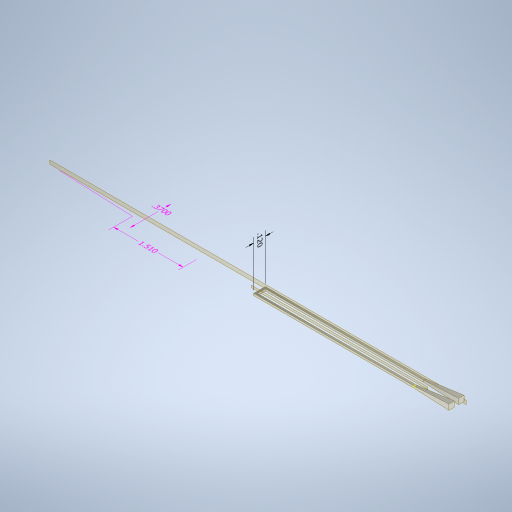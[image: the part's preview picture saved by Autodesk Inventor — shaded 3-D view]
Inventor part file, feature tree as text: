
AUTODESK INVENTOR PART (.ipt)
format: ipt  version: 2024.2 (Build 282272000, 272)  size: 313,856 bytes
history: native  units: in
note: dims shown in document units (in); Inventor stores cm internally (conversion verified against a paired STEP export)
features: other x5, plane x4, sketch x4, sweep x1, loft x1, mirror x1, projected_geometry x1
ambient origin geometry x8: Origin, YZ Plane, XZ Plane, XY Plane, X Axis, Y Axis, Z Axis, Center Point
bodies: Solid1 (feature_tree)
feature tree (17):
  other  "Annotations"
  sweep  "Sweep1"
  plane  "Work Plane1"
  plane  "Work Plane2"
  plane  "Work Plane4"
  sketch  "Sketch15"  dims[d86=-0.1175in]
  sketch  "Sketch16"  dims[d89=0.1in d90=0.0in d91=0.0in d92=0.0in d98=0.02in d99=0.02in d100=0.055in d102=0.055in d104=0.0in d109=0.0in d110=90.0deg d111=0.0in d112=90.0deg d116=-0.06in d113=0.0in d114=0.3937in d115=0.12in d42=0.2341in d43=0.169in d44=0.37in d48=0.2141in d49=0.2512in d50=1.51in]
  loft  "Loft3"
  plane  "Work Plane5"
  mirror  "Mirror3"
  sketch  "Sketch1"  dims[d6=0.0in d7=0.0in d11=0.375in d19=-0.25in]
  sketch  "Sketch2"  dims[d69=1.625in d70=1.625in]
  projected_geometry  "Projected Loop1"
  other  "Edges4"
  other  "Linear Dimension 1"
  other  "Linear Dimension 3"
  other  "Linear Dimension 4"
